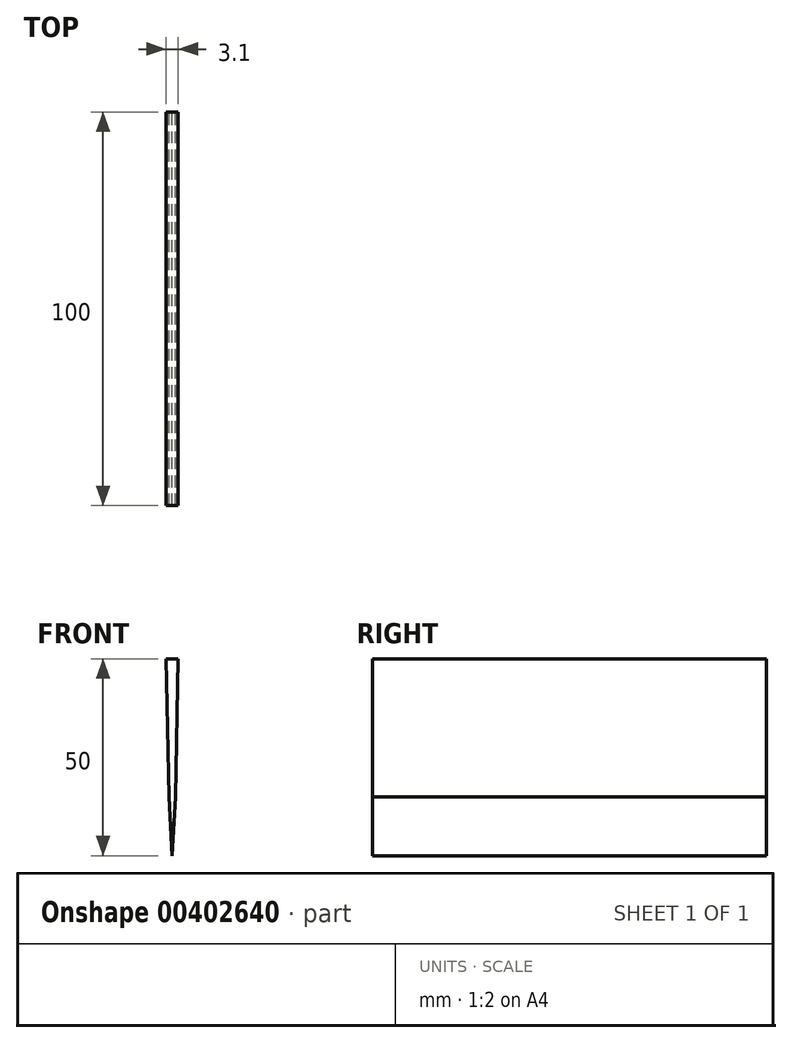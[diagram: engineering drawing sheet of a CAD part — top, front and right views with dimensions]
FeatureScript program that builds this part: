
annotation { "Feature Type Name" : "Feature", "Feature Type Description" : "" }
export const myFeature = defineFeature(function(context is Context, id is Id, definition is map)
    precondition{}
    {
        {
            var Q0;
            Q0=qCreatedBy(makeId("Front.planeOp"),FACE);
            var sketch = newSketch(context, id + "F0", { "sketchPlane" : qUnion([Q0])});
            skLineSegment(sketch, "E0", {"start": v(-1.55, 35) * mm, "end": v(1.55, 35) * mm});
            skLineSegment(sketch, "E1", {"start": v(1.55, 35) * mm, "end": v(0.8, 0) * mm});
            skLineSegment(sketch, "E2", {"start": v(0.8, 0) * mm, "end": v(0, -15) * mm});
            skLineSegment(sketch, "E3", {"start": v(0, -15) * mm, "end": v(-0.8, 0) * mm});
            skLineSegment(sketch, "E4", {"start": v(-0.8, 0) * mm, "end": v(-1.55, 35) * mm});
            skSolve(sketch);
        }
        {
            var Q0;
            Q0=makeQuery(id+"F0.imprint","IMPRINT",FACE,{"disambiguationData":[TD([[makeQuery(id+"F0.imprint","IMPRINT",EDGE,{"derivedFrom":sQuery(id+"F0.wireOp",EDGE,"E0")}),-1.0]])]});
            extrude(context, id + "F1", {"entities" : qUnion([Q0]), "depth" : 100 * mm, "offsetDistance" : 25 * mm});
        }
    });
